MODEL slx_f5f0259db59d
CONFIG AbsTol = auto
CONFIG EnableMultiTasking = off
CONFIG FixedStep = auto
CONFIG MaxStep = auto
CONFIG MinStep = auto
CONFIG RelTol = 1e-3
CONFIG SampleTimeConstraint = Unconstrained
CONFIG SolverName = VariableStepAuto
CONFIG StartTime = 0.0
CONFIG StopTime = 8
BLOCK [Reference] AC Voltage Source3  REF=spsACVoltageSourceLib/AC Voltage Source
  LibrarySourceBlock = sps_lib/Sources/AC Voltage Source
  SourceBlock = spsACVoltageSourceLib/AC Voltage Source
  SourceType = AC Voltage Source
BLOCK [SubSystem] Brake Selector
BLOCK [From] Brake Selector/From1
  GotoTag = Brake
  TagVisibility = global
BLOCK [Inport] Brake Selector/Normally Close
  IconDisplay = Signal name
  Port = 2
BLOCK [Inport] Brake Selector/Normally Open
  IconDisplay = Signal name
BLOCK [Outport] Brake Selector/Out
  IconDisplay = Signal name
BLOCK [Switch] Brake Selector/Switch1
  InputSameDT = off
  SaturateOnIntegerOverflow = off
  Threshold = 0.5
BLOCK [SubSystem] Brake Selector1
BLOCK [From] Brake Selector1/From1
  GotoTag = Brake
  TagVisibility = global
BLOCK [Inport] Brake Selector1/Normally Close
  IconDisplay = Signal name
  Port = 2
BLOCK [Inport] Brake Selector1/Normally Open
  IconDisplay = Signal name
BLOCK [Outport] Brake Selector1/Out
  IconDisplay = Signal name
BLOCK [Switch] Brake Selector1/Switch1
  InputSameDT = off
  SaturateOnIntegerOverflow = off
  Threshold = 0.5
BLOCK [SubSystem] Brake Selector2
BLOCK [From] Brake Selector2/From1
  GotoTag = Brake
  TagVisibility = global
BLOCK [Inport] Brake Selector2/Normally Close
  IconDisplay = Signal name
  Port = 2
BLOCK [Inport] Brake Selector2/Normally Open
  IconDisplay = Signal name
BLOCK [Outport] Brake Selector2/Out
  IconDisplay = Signal name
BLOCK [Switch] Brake Selector2/Switch1
  InputSameDT = off
  SaturateOnIntegerOverflow = off
  Threshold = 0.5
BLOCK [SubSystem] Brake Selector3
BLOCK [From] Brake Selector3/From1
  GotoTag = Brake
  TagVisibility = global
BLOCK [Inport] Brake Selector3/Normally Close
  IconDisplay = Signal name
  Port = 2
BLOCK [Inport] Brake Selector3/Normally Open
  IconDisplay = Signal name
BLOCK [Outport] Brake Selector3/Out
  IconDisplay = Signal name
BLOCK [Switch] Brake Selector3/Switch1
  InputSameDT = off
  SaturateOnIntegerOverflow = off
  Threshold = 0.5
BLOCK [BusSelector] Bus Selector1
  OutputSignals = Electrical torque Te (n m),Speed wm (rad/s)
BLOCK [Constant] CCW Direction
  Value = 0
BLOCK [Constant] CW Direction
BLOCK [Constant] Constant
  Value = 0
BLOCK [Constant] Constant1
BLOCK [Constant] Constant2
  Value = 0.6
BLOCK [Constant] Constant3
BLOCK [Constant] Constant4
  Value = 0
BLOCK [Reference] Current Measurement  REF=spsCurrentMeasurementLib/Current Measurement
  LibrarySourceBlock = sps_lib/Sensors and Measurements/Current Measurement
  SourceBlock = spsCurrentMeasurementLib/Current Measurement
  SourceType = Current Measurement
  UserDataPersistent = on
BLOCK [Reference] Current Measurement1  REF=spsCurrentMeasurementLib/Current Measurement
  LibrarySourceBlock = sps_lib/Sensors and Measurements/Current Measurement
  SourceBlock = spsCurrentMeasurementLib/Current Measurement
  SourceType = Current Measurement
  UserDataPersistent = on
BLOCK [Reference] Current Measurement2  REF=spsCurrentMeasurementLib/Current Measurement
  LibrarySourceBlock = sps_lib/Sensors and Measurements/Current Measurement
  SourceBlock = spsCurrentMeasurementLib/Current Measurement
  SourceType = Current Measurement
  UserDataPersistent = on
BLOCK [Reference] Current Measurement3  REF=spsCurrentMeasurementLib/Current Measurement
  LibrarySourceBlock = sps_lib/Sensors and Measurements/Current Measurement
  NameLocation = right
  SourceBlock = spsCurrentMeasurementLib/Current Measurement
  SourceType = Current Measurement
  UserDataPersistent = on
BLOCK [Reference] Current Measurement4  REF=spsCurrentMeasurementLib/Current Measurement
  Commented = on
  LibrarySourceBlock = sps_lib/Sensors and Measurements/Current Measurement
  NameLocation = left
  SourceBlock = spsCurrentMeasurementLib/Current Measurement
  SourceType = Current Measurement
  UserDataPersistent = on
BLOCK [Reference] Current Measurement5  REF=spsCurrentMeasurementLib/Current Measurement
  LibrarySourceBlock = sps_lib/Sensors and Measurements/Current Measurement
  NameLocation = left
  SourceBlock = spsCurrentMeasurementLib/Current Measurement
  SourceType = Current Measurement
  UserDataPersistent = on
BLOCK [Reference] DC Machine1  REF=spsDCMachineLib/DC Machine
  LibrarySourceBlock = sps_lib/Electrical Machines/DC Machine
  SourceBlock = spsDCMachineLib/DC Machine
  SourceType = DC machine
BLOCK [Reference] DC Voltage Source  REF=spsDCVoltageSourceLib/DC Voltage Source
  LibrarySourceBlock = sps_lib/Sources/DC Voltage Source
  NameLocation = right
  SourceBlock = spsDCVoltageSourceLib/DC Voltage Source
  SourceType = DC Voltage Source
BLOCK [Reference] DC Voltage Source1  REF=spsDCVoltageSourceLib/DC Voltage Source
  Commented = on
  LibrarySourceBlock = sps_lib/Sources/DC Voltage Source
  SourceBlock = spsDCVoltageSourceLib/DC Voltage Source
  SourceType = DC Voltage Source
BLOCK [Reference] Diode1  REF=spsDiodeLib/Diode
  LibrarySourceBlock = sps_lib/Power Electronics/Diode
  NameLocation = right
  SourceBlock = spsDiodeLib/Diode
  SourceType = Diode
BLOCK [Reference] Diode2  REF=spsDiodeLib/Diode
  LibrarySourceBlock = sps_lib/Power Electronics/Diode
  NameLocation = right
  SourceBlock = spsDiodeLib/Diode
  SourceType = Diode
BLOCK [Reference] Diode3  REF=spsDiodeLib/Diode
  LibrarySourceBlock = sps_lib/Power Electronics/Diode
  NameLocation = right
  SourceBlock = spsDiodeLib/Diode
  SourceType = Diode
BLOCK [Reference] Diode4  REF=spsDiodeLib/Diode
  LibrarySourceBlock = sps_lib/Power Electronics/Diode
  NameLocation = right
  SourceBlock = spsDiodeLib/Diode
  SourceType = Diode
BLOCK [Reference] Diode5  REF=spsDiodeLib/Diode
  LibrarySourceBlock = sps_lib/Power Electronics/Diode
  NameLocation = right
  SourceBlock = spsDiodeLib/Diode
  SourceType = Diode
BLOCK [Reference] Diode6  REF=spsDiodeLib/Diode
  LibrarySourceBlock = sps_lib/Power Electronics/Diode
  NameLocation = right
  SourceBlock = spsDiodeLib/Diode
  SourceType = Diode
BLOCK [Reference] Diode7  REF=spsDiodeLib/Diode
  LibrarySourceBlock = sps_lib/Power Electronics/Diode
  NameLocation = right
  SourceBlock = spsDiodeLib/Diode
  SourceType = Diode
BLOCK [Reference] Diode8  REF=spsDiodeLib/Diode
  LibrarySourceBlock = sps_lib/Power Electronics/Diode
  NameLocation = right
  SourceBlock = spsDiodeLib/Diode
  SourceType = Diode
BLOCK [Display] Display
  Decimation = 1
BLOCK [Display] Display1
  Decimation = 1
BLOCK [Display] Display2
  Decimation = 1
BLOCK [Display] Display3
  Decimation = 1
BLOCK [Display] Display4
  Decimation = 1
BLOCK [Reference] First-Order Filter  REF=spsFirstOrderFilterLib/First-Order
Filter
  LibrarySourceBlock = sps_lib/Control/Filters/First-Order
Filter
  SourceBlock = spsFirstOrderFilterLib/First-Order
Filter
  SourceType = First-Order Filter
BLOCK [From] From
  GotoTag = Gate_Q1
  NameLocation = left
BLOCK [From] From1
  GotoTag = Gate_Q3
  NameLocation = left
BLOCK [From] From2
  GotoTag = Gate_Q4
  NameLocation = left
BLOCK [From] From3
  GotoTag = Gate_Q2
  NameLocation = left
BLOCK [From] From4
  GotoTag = Gate_Q1
BLOCK [From] From5
  GotoTag = Gate_Q2
BLOCK [From] From6
  GotoTag = Gate_Q3
BLOCK [From] From7
  GotoTag = Gate_Q4
BLOCK [From] From8
  GotoTag = Torque
  NameLocation = left
BLOCK [Scope] Gate Signals
  ActiveDisplayYMaximum = 1.2434958153271063
  ActiveDisplayYMinimum = -0.0065041846728933761
  DataLoggingVariableName = ScopeData21
  Floating = off
  GraphicalSettings = {"Style":{"BackgroundColor":[0.12941176470588237,0.12941176470588237,0.12941176470588237],"AxesColor":[0.07058823529411765,0.07058823529411765,0.07058823529411765],"LabelsColor":[0.8509803921568627,0.8509803921568627,0.8509803921568627],"PreserveColors":false,"Visible":[false,true,false,true],"LineStyle":["-","-","-","-"],"LineWidth":[1.5,1.5,1.5,1.5],"BarWidth":[0.9,0.9,0.9,0.9],"LineColor":["aut...<+2324ch>
  MultipleDisplayCache = [{"MaxYLimMag":1.125,"MaxYLimReal":1.2434958153271063,"MinYLimMag":0,"MinYLimReal":-0.0065041846728933761,"PlotAsMagnitudePhase":false,"ShowGrid":true,"ShowLegend":true,"Title":"%<SignalLabel>","YLabel":""}]
  NumInputPorts = 4
  ScopeFrameLocation = window
  ShowLegend = on
  WasSavedAsWebScope = on
  WindowPosition = [920.000000,418.000000,826.000000,527.000000,]
BLOCK [Goto] Goto
  GotoTag = Brake
  TagVisibility = global
BLOCK [Goto] Goto1
  GotoTag = Gate_Q1
BLOCK [Goto] Goto2
  GotoTag = Gate_Q3
BLOCK [Goto] Goto3
  GotoTag = Torque
BLOCK [Goto] Goto4
  GotoTag = Gate_Q2
BLOCK [Goto] Goto5
  GotoTag = Gate_Q4
BLOCK [Reference] Ground  REF=spsGroundLib/Ground
  LibrarySourceBlock = sps_lib/Utilities/Ground
  NameLocation = right
  SourceBlock = spsGroundLib/Ground
  SourceType = Ground
BLOCK [ManualSwitch] Manual Switch
BLOCK [ManualSwitch] Manual Switch1
  CurrentSetting = 0
BLOCK [ManualSwitch] Manual Switch2
BLOCK [Reference] Manual Variant Sink  REF=simulink/Signal
Routing/Manual
Variant Sink
  NameLocation = left
  SourceBlock = simulink/Signal
Routing/Manual
Variant Sink
  SourceType = ManualVariantSink
BLOCK [Reference] Mean  REF=spsMeanLib/Mean
  LibrarySourceBlock = sps_lib/Sensors and Measurements/Mean
  SourceBlock = spsMeanLib/Mean
  SourceType = Mean
BLOCK [Reference] Mean1  REF=spsMeanLib/Mean
  LibrarySourceBlock = sps_lib/Sensors and Measurements/Mean
  SourceBlock = spsMeanLib/Mean
  SourceType = Mean
BLOCK [Reference] Mean2  REF=spsMeanLib/Mean
  LibrarySourceBlock = sps_lib/Sensors and Measurements/Mean
  SourceBlock = spsMeanLib/Mean
  SourceType = Mean
BLOCK [Reference] Mean3  REF=spsMeanLib/Mean
  LibrarySourceBlock = sps_lib/Sensors and Measurements/Mean
  SourceBlock = spsMeanLib/Mean
  SourceType = Mean
BLOCK [Reference] Mosfet5  REF=spsMosfetLib/Mosfet
  LibrarySourceBlock = sps_lib/Power Electronics/Mosfet
  NameLocation = left
  SourceBlock = spsMosfetLib/Mosfet
  SourceType = Mosfet
BLOCK [Logic] NOT
  AllPortsSameDT = off
  IconShape = distinctive
  Operator = NOT
  OutDataTypeStr = boolean
BLOCK [Reference] PWM Generator  REF=eePwmGenerator/PWM Generator
  LibrarySourceBlock = ee_sl_lib/Pulse Width
Modulation/PWM Generator
  SourceBlock = eePwmGenerator/PWM Generator
  SourceType = PWM Generator
BLOCK [Reference] PWM Generator1  REF=eePwmGenerator/PWM Generator
  LibrarySourceBlock = ee_sl_lib/Pulse Width
Modulation/PWM Generator
  SourceBlock = eePwmGenerator/PWM Generator
  SourceType = PWM Generator
BLOCK [Product] Product
BLOCK [Product] Product1
BLOCK [Product] Product2
BLOCK [Product] Product3
BLOCK [Product] Product4
BLOCK [Product] Product5
BLOCK [Reference] Q1  REF=spsMosfetLib/Mosfet
  LibrarySourceBlock = sps_lib/Power Electronics/Mosfet
  NameLocation = left
  SourceBlock = spsMosfetLib/Mosfet
  SourceType = Mosfet
BLOCK [Reference] Q2  REF=spsMosfetLib/Mosfet
  LibrarySourceBlock = sps_lib/Power Electronics/Mosfet
  NameLocation = left
  SourceBlock = spsMosfetLib/Mosfet
  SourceType = Mosfet
BLOCK [Reference] Q3  REF=spsMosfetLib/Mosfet
  LibrarySourceBlock = sps_lib/Power Electronics/Mosfet
  NameLocation = left
  SourceBlock = spsMosfetLib/Mosfet
  SourceType = Mosfet
BLOCK [Reference] Q4  REF=spsMosfetLib/Mosfet
  LibrarySourceBlock = sps_lib/Power Electronics/Mosfet
  NameLocation = left
  SourceBlock = spsMosfetLib/Mosfet
  SourceType = Mosfet
BLOCK [Reference] Ramp  REF=simulink/Sources/Ramp
  SourceBlock = simulink/Sources/Ramp
  SourceType = Ramp
BLOCK [Reference] Ramp1  REF=simulink/Sources/Ramp
  SourceBlock = simulink/Sources/Ramp
  SourceType = Ramp
BLOCK [Reference] Ramp2  REF=simulink/Sources/Ramp
  SourceBlock = simulink/Sources/Ramp
  SourceType = Ramp
BLOCK [Saturate] Saturation
  LowerLimit = 0
  UpperLimit = 20
BLOCK [Saturate] Saturation1
  LowerLimit = 0
  UpperLimit = 0.8
BLOCK [Saturate] Saturation2
  LowerLimit = 0
  UpperLimit = 1
BLOCK [Scope] Scope
  ActiveDisplayYMaximum = 104.1740277954152
  ActiveDisplayYMinimum = -11.583479260065536
  DataLoggingVariableName = ScopeData2
  Floating = off
  GraphicalSettings = {"AxesScalingProperties":{"AlignXAxis":"Center","AlignYAxis":"Center","AutoScaleXAxisLimits":false,"AxesScaling":"Manual","AxesScalingNumUpdates":10,"ExpandOnly":true,"ScaleAxesLimitsAtStop":false,"XAxisDataRange":100,"YAxisDataRange":80},"DisplayProperties":{"ColorOrder":["auto","auto","auto","auto","auto","auto","auto","auto","auto","auto","auto","auto","auto","auto","auto","auto","auto","auto",...<+2160ch>
  MultipleDisplayCache = [{"MaxYLimMag":104.1740277954152,"MaxYLimReal":104.1740277954152,"MinYLimMag":0,"MinYLimReal":-11.583479260065536,"PlotAsMagnitudePhase":false,"ShowGrid":true,"ShowLegend":true,"Title":"%<SignalLabel>","YLabel":""}]
  NameLocation = left
  NumInputPorts = 1
  ScopeFrameLocation = window
  ShowLegend = on
  Visible = on
  WasSavedAsWebScope = on
  WindowPosition = [0.000000,32.000000,1920.000000,1017.000000,]
BLOCK [Scope] Scope1
  ActiveDisplayYMaximum = 256.22277966423093
  ActiveDisplayYMinimum = -28.46919774047009
  Floating = off
  GraphicalSettings = {"AxesScalingProperties":{"AlignXAxis":"Center","AlignYAxis":"Center","AutoScaleXAxisLimits":false,"AxesScaling":"Manual","AxesScalingNumUpdates":10,"ExpandOnly":true,"ScaleAxesLimitsAtStop":false,"XAxisDataRange":100,"YAxisDataRange":80},"DisplayProperties":{"ColorOrder":["auto","auto","auto","auto","auto","auto","auto","auto","auto","auto","auto","auto","auto","auto","auto","auto","auto","auto",...<+2032ch>  <repeated x3 — deduplicated>
  MultipleDisplayCache = [{"MaxYLimMag":256.22277966423093,"MaxYLimReal":256.22277966423093,"MinYLimMag":0,"MinYLimReal":-28.46919774047009,"PlotAsMagnitudePhase":false,"ShowGrid":true,"ShowLegend":false,"Title":"%<SignalLabel>","YLabel":""}]
  NumInputPorts = 1
  ScopeFrameLocation = window
  WasSavedAsWebScope = on
  WindowPosition = [1.000000,41.000000,1920.000000,1017.000000,]
BLOCK [Scope] Scope10
  ActiveDisplayYMaximum = 1429.223755324701
  ActiveDisplayYMinimum = 624.50186928798541
  DataLoggingVariableName = ScopeData10
  Floating = off
  GraphicalSettings = {"AxesScalingProperties":{"AlignXAxis":"Center","AlignYAxis":"Center","AutoScaleXAxisLimits":false,"AxesScaling":"Manual","AxesScalingNumUpdates":10,"ExpandOnly":true,"ScaleAxesLimitsAtStop":false,"XAxisDataRange":100,"YAxisDataRange":80},"DisplayProperties":{"ColorOrder":["auto","auto","auto","auto","auto","auto","auto","auto","auto","auto","auto","auto","auto","auto","auto","auto","auto","auto",...<+1914ch>
  MultipleDisplayCache = [{"MaxYLimMag":3801.8138292180056,"MaxYLimReal":1429.223755324701,"MinYLimMag":0,"MinYLimReal":624.50186928798541,"PlotAsMagnitudePhase":false,"ShowGrid":true,"ShowLegend":false,"Title":"%<SignalLabel>","YLabel":""}]
  NumInputPorts = 1
  ScopeFrameLocation = window
  WasSavedAsWebScope = on
  WindowPosition = [1.000000,41.000000,1920.000000,1017.000000,]
BLOCK [Scope] Scope11
  ActiveDisplayYMaximum = 10839.355284849147
  ActiveDisplayYMinimum = -2401.1873049076858
  DataLoggingVariableName = ScopeData12
  Floating = off
  GraphicalSettings = {"AxesScalingProperties":{"AlignXAxis":"Center","AlignYAxis":"Center","AutoScaleXAxisLimits":false,"AxesScaling":"Manual","AxesScalingNumUpdates":10,"ExpandOnly":true,"ScaleAxesLimitsAtStop":false,"XAxisDataRange":100,"YAxisDataRange":80},"DisplayProperties":{"ColorOrder":["auto","auto","auto","auto","auto","auto","auto","auto","auto","auto","auto","auto","auto","auto","auto","auto","auto","auto",...<+2024ch>
  MultipleDisplayCache = [{"MaxYLimMag":23271.969727015163,"MaxYLimReal":10839.355284849147,"MinYLimMag":0,"MinYLimReal":-2401.1873049076858,"PlotAsMagnitudePhase":false,"ShowGrid":true,"ShowLegend":false,"Title":"%<SignalLabel>","YLabel":""}]
  NumInputPorts = 1
  ScopeFrameLocation = window
  WasSavedAsWebScope = on
  WindowPosition = [783.000000,533.000000,560.000000,420.000000,]
BLOCK [Scope] Scope12
  ActiveDisplayYMaximum = 104.03628291708009
  ActiveDisplayYMinimum = -11.566622282825097
  DataLoggingVariableName = ScopeData11
  Floating = off
  GraphicalSettings = {"Style":{"BackgroundColor":[0.12941176470588237,0.12941176470588237,0.12941176470588237],"AxesColor":[0.07058823529411765,0.07058823529411765,0.07058823529411765],"LabelsColor":[0.8509803921568627,0.8509803921568627,0.8509803921568627],"PreserveColors":false,"Visible":[true],"LineStyle":["-"],"LineWidth":[1.5],"BarWidth":[0.9],"LineColor":["auto"],"LineFaceAlpha":[1],"LineEdgeAlpha":[1],"Marker":...<+2017ch>
  MultipleDisplayCache = [{"MaxYLimMag":104.03628291708009,"MaxYLimReal":104.03628291708009,"MinYLimMag":0,"MinYLimReal":-11.566622282825097,"PlotAsMagnitudePhase":false,"ShowGrid":true,"ShowLegend":false,"Title":"%<SignalLabel>","YLabel":""}]
  NameLocation = right
  NumInputPorts = 1
  ScopeFrameLocation = window
  WasSavedAsWebScope = on
  WindowPosition = [0.000000,32.000000,1536.000000,801.000000,]
BLOCK [Scope] Scope13
  DataLoggingVariableName = ScopeData13
  Floating = off
  GraphicalSettings = {"GraphicalSettings":{"LegacySettings":true,"Style":{"Style":{"PlotType":"Auto"}}}}
  NumInputPorts = 1
  WasSavedAsWebScope = on
BLOCK [Scope] Scope14
  ActiveDisplayYMaximum = 2945.0127128560962
  ActiveDisplayYMinimum = 762.41218453396561
  DataLoggingVariableName = ScopeData14
  Floating = off
  GraphicalSettings = {"AxesScalingProperties":{"AlignXAxis":"Center","AlignYAxis":"Center","AutoScaleXAxisLimits":false,"AxesScaling":"Manual","AxesScalingNumUpdates":10,"ExpandOnly":true,"ScaleAxesLimitsAtStop":false,"XAxisDataRange":100,"YAxisDataRange":80},"DisplayProperties":{"ColorOrder":["auto","auto","auto","auto","auto","auto","auto","auto","auto","auto","auto","auto","auto","auto","auto","auto","auto","auto",...<+2026ch>
  MultipleDisplayCache = [{"MaxYLimMag":23271.969727015163,"MaxYLimReal":2945.0127128560962,"MinYLimMag":0,"MinYLimReal":762.41218453396561,"PlotAsMagnitudePhase":false,"ShowGrid":true,"ShowLegend":false,"Title":"%<SignalLabel>","YLabel":""}]
  NumInputPorts = 1
  ScopeFrameLocation = window
  WasSavedAsWebScope = on
  WindowPosition = [1.000000,41.000000,1920.000000,1017.000000,]
BLOCK [Scope] Scope15
  DataLoggingVariableName = ScopeData15
  Floating = off
  GraphicalSettings = {"GraphicalSettings":{"LegacySettings":true,"Style":{"Style":{"PlotType":"Auto"}}}}
  NumInputPorts = 1
  WasSavedAsWebScope = on
BLOCK [Scope] Scope16
  ActiveDisplayYMaximum = 137.54032935552146
  ActiveDisplayYMinimum = -15.282258817280159
  DataLoggingVariableName = ScopeData16
  Floating = off
  GraphicalSettings = {"Style":{"BackgroundColor":[0.12941176470588237,0.12941176470588237,0.12941176470588237],"AxesColor":[0.07058823529411765,0.07058823529411765,0.07058823529411765],"LabelsColor":[0.8509803921568627,0.8509803921568627,0.8509803921568627],"PreserveColors":false,"Visible":[true],"LineStyle":["-"],"LineWidth":[1.5],"BarWidth":[0.9],"LineColor":["auto"],"LineFaceAlpha":[1],"LineEdgeAlpha":[1],"Marker":...<+2338ch>
  MultipleDisplayCache = [{"MaxYLimMag":137.54032935552146,"MaxYLimReal":137.54032935552146,"MinYLimMag":0,"MinYLimReal":-15.282258817280159,"PlotAsMagnitudePhase":false,"ShowGrid":true,"ShowLegend":false,"Title":"%<SignalLabel>","YLabel":""}]
  NumInputPorts = 1
  ScopeFrameLocation = window
  WasSavedAsWebScope = on
  WindowPosition = [2.000000,42.000000,1918.000000,1008.000000,]
BLOCK [Scope] Scope17
  ActiveDisplayYMaximum = 226.2370362043749
  ActiveDisplayYMinimum = -36.761209497993441
  DataLoggingVariableName = ScopeData17
  Floating = off
  GraphicalSettings = {"Style":{"BackgroundColor":[0.12941176470588237,0.12941176470588237,0.12941176470588237],"AxesColor":[0.07058823529411765,0.07058823529411765,0.07058823529411765],"LabelsColor":[0.8509803921568627,0.8509803921568627,0.8509803921568627],"PreserveColors":false,"Visible":[true],"LineStyle":["-"],"LineWidth":[1.5],"BarWidth":[0.9],"LineColor":["auto"],"LineFaceAlpha":[1],"LineEdgeAlpha":[1],"Marker":...<+2019ch>
  MultipleDisplayCache = [{"MaxYLimMag":226.2370362043749,"MaxYLimReal":226.2370362043749,"MinYLimMag":0,"MinYLimReal":-36.761209497993441,"PlotAsMagnitudePhase":false,"ShowGrid":true,"ShowLegend":false,"Title":"%<SignalLabel>","YLabel":""}]
  NumInputPorts = 1
  ScopeFrameLocation = window
  WasSavedAsWebScope = on
  WindowPosition = [2.000000,42.000000,1918.000000,1008.000000,]
BLOCK [Scope] Scope18
  DataLoggingVariableName = ScopeData18
  Floating = off
  GraphicalSettings = {"GraphicalSettings":{"LegacySettings":true,"Style":{"Style":{"PlotType":"Auto"}}}}
  NameLocation = left
  NumInputPorts = 1
  WasSavedAsWebScope = on
BLOCK [Scope] Scope19
  ActiveDisplayYMaximum = 103.81128270332889
  ActiveDisplayYMinimum = -12.603657312689416
  DataLoggingVariableName = ScopeData19
  Floating = off
  GraphicalSettings = {"Style":{"BackgroundColor":[0.12941176470588237,0.12941176470588237,0.12941176470588237],"AxesColor":[0.07058823529411765,0.07058823529411765,0.07058823529411765],"LabelsColor":[0.8509803921568627,0.8509803921568627,0.8509803921568627],"PreserveColors":false,"Visible":[true],"LineStyle":["-"],"LineWidth":[1.5],"BarWidth":[0.9],"LineColor":["auto"],"LineFaceAlpha":[1],"LineEdgeAlpha":[1],"Marker":...<+1920ch>
  MultipleDisplayCache = [{"MaxYLimMag":103.81128270332889,"MaxYLimReal":103.81128270332889,"MinYLimMag":0,"MinYLimReal":-12.603657312689416,"PlotAsMagnitudePhase":false,"ShowGrid":true,"ShowLegend":false,"Title":"%<SignalLabel>","YLabel":""}]
  NameLocation = top
  NumInputPorts = 1
  ScopeFrameLocation = window
  WasSavedAsWebScope = on
  WindowPosition = [680.000000,330.000000,560.000000,420.000000,]
BLOCK [Scope] Scope2
  ActiveDisplayYMaximum = 25.20951403026401
  ActiveDisplayYMinimum = -226.88562627237616
  DataLoggingVariableName = ScopeData3
  Floating = off
  GraphicalSettings = {"Style":{"BackgroundColor":[0.12941176470588237,0.12941176470588237,0.12941176470588237],"AxesColor":[0.07058823529411765,0.07058823529411765,0.07058823529411765],"LabelsColor":[0.8509803921568627,0.8509803921568627,0.8509803921568627],"PreserveColors":false,"Visible":[true,true],"LineStyle":["-","-"],"LineWidth":[1.5,1.5],"BarWidth":[0.9,0.9],"LineColor":["auto","auto"],"LineFaceAlpha":[1,1],"Li...<+2069ch>
  MultipleDisplayCache = [{"MaxYLimMag":226.88562627237616,"MaxYLimReal":25.20951403026401,"MinYLimMag":0,"MinYLimReal":-226.88562627237616,"PlotAsMagnitudePhase":false,"ShowGrid":true,"ShowLegend":false,"Title":"%<SignalLabel>","YLabel":""}]
  NameLocation = right
  NumInputPorts = 1
  ScopeFrameLocation = window
  WasSavedAsWebScope = on
  WindowPosition = [488.000000,222.000000,560.000000,420.000000,]
BLOCK [Scope] Scope20
  ActiveDisplayYMaximum = 1.125
  ActiveDisplayYMinimum = -0.12499999999999997
  DataLoggingVariableName = ScopeData20
  Floating = off
  GraphicalSettings = {"AxesScalingProperties":{"AlignXAxis":"Center","AlignYAxis":"Center","AutoScaleXAxisLimits":false,"AxesScaling":"Manual","AxesScalingNumUpdates":10,"ExpandOnly":true,"ScaleAxesLimitsAtStop":false,"XAxisDataRange":100,"YAxisDataRange":80},"DisplayProperties":{"ColorOrder":["auto","auto","auto","auto","auto","auto","auto","auto","auto","auto","auto","auto","auto","auto","auto","auto","auto","auto",...<+1970ch>
  MultipleDisplayCache = [{"MaxYLimMag":1.125,"MaxYLimReal":1.125,"MinYLimMag":0,"MinYLimReal":-0.12499999999999997,"PlotAsMagnitudePhase":false,"ShowGrid":true,"ShowLegend":false,"Title":"%<SignalLabel>","YLabel":""}]
  NumInputPorts = 1
  ScopeFrameLocation = window
  WasSavedAsWebScope = on
  WindowPosition = [1.000000,41.000000,1920.000000,1017.000000,]
BLOCK [Scope] Scope21
  ActiveDisplayYMaximum = 211.04566043540314
  ActiveDisplayYMinimum = -1899.3717072203649
  DataLoggingVariableName = ScopeData9
  Floating = off
  GraphicalSettings = {"AxesScalingProperties":{"AlignXAxis":"Center","AlignYAxis":"Center","AutoScaleXAxisLimits":false,"AxesScaling":"Manual","AxesScalingNumUpdates":10,"ExpandOnly":true,"ScaleAxesLimitsAtStop":false,"XAxisDataRange":100,"YAxisDataRange":80},"DisplayProperties":{"ColorOrder":["auto","auto","auto","auto","auto","auto","auto","auto","auto","auto","auto","auto","auto","auto","auto","auto","auto","auto",...<+2205ch>
  MultipleDisplayCache = [{"MaxYLimMag":1899.3717072203649,"MaxYLimReal":211.04566043540314,"MinYLimMag":0,"MinYLimReal":-1899.3717072203649,"PlotAsMagnitudePhase":false,"ShowGrid":true,"ShowLegend":false,"Title":"%<SignalLabel>","YLabel":""}]
  NumInputPorts = 1
  ScopeFrameLocation = window
  WasSavedAsWebScope = on
  WindowPosition = [1.000000,41.000000,1920.000000,1017.000000,]
BLOCK [Scope] Scope22
  ActiveDisplayYMaximum = 43.751360629299874
  ActiveDisplayYMinimum = -4.8702002164060625
  DataLoggingVariableName = ScopeData23
  Floating = off
  GraphicalSettings = {"Style":{"BackgroundColor":[0.12941176470588237,0.12941176470588237,0.12941176470588237],"AxesColor":[0.07058823529411765,0.07058823529411765,0.07058823529411765],"LabelsColor":[0.8509803921568627,0.8509803921568627,0.8509803921568627],"PreserveColors":false,"Visible":[true],"LineStyle":["-"],"LineWidth":[1.5],"BarWidth":[0.9],"LineColor":["auto"],"LineFaceAlpha":[1],"LineEdgeAlpha":[1],"Marker":...<+2025ch>
  MultipleDisplayCache = [{"MaxYLimMag":43.751360629299874,"MaxYLimReal":43.751360629299874,"MinYLimMag":0,"MinYLimReal":-4.8702002164060625,"PlotAsMagnitudePhase":false,"ShowGrid":true,"ShowLegend":false,"Title":"%<SignalLabel>","YLabel":""}]
  NameLocation = right
  NumInputPorts = 1
  ScopeFrameLocation = window
  WasSavedAsWebScope = on
  WindowPosition = [1.000000,41.000000,1920.000000,1017.000000,]
BLOCK [Scope] Scope23
  ActiveDisplayYMaximum = 71.245138524934077
  ActiveDisplayYMinimum = -145.42462200714976
  Commented = on
  DataLoggingVariableName = ScopeData24
  Floating = off
  GraphicalSettings = {"AxesScalingProperties":{"AlignXAxis":"Center","AlignYAxis":"Center","AutoScaleXAxisLimits":false,"AxesScaling":"Manual","AxesScalingNumUpdates":10,"ExpandOnly":true,"ScaleAxesLimitsAtStop":false,"XAxisDataRange":100,"YAxisDataRange":80},"DisplayProperties":{"ColorOrder":["auto","auto","auto","auto","auto","auto","auto","auto","auto","auto","auto","auto","auto","auto","auto","auto","auto","auto",...<+1936ch>
  MultipleDisplayCache = [{"MaxYLimMag":145.42462200714976,"MaxYLimReal":71.245138524934077,"MinYLimMag":0,"MinYLimReal":-145.42462200714976,"PlotAsMagnitudePhase":false,"ShowGrid":true,"ShowLegend":false,"Title":"%<SignalLabel>","YLabel":""}]
  NumInputPorts = 1
  ScopeFrameLocation = window
  WasSavedAsWebScope = on
  WindowPosition = [1.000000,41.000000,1920.000000,1017.000000,]
BLOCK [Scope] Scope24
  ActiveDisplayYMaximum = 197.18570910939735
  ActiveDisplayYMinimum = -110.97493026864629
  DataLoggingVariableName = ScopeData25
  Floating = off
  MultipleDisplayCache = [{"MaxYLimMag":184.87259500897878,"MaxYLimReal":197.18570910939735,"MinYLimMag":0,"MinYLimReal":-110.97493026864629,"PlotAsMagnitudePhase":false,"ShowGrid":true,"ShowLegend":false,"Title":"%<SignalLabel>","YLabel":""}]
  NameLocation = top
  NumInputPorts = 1
  ScopeFrameLocation = window
  WasSavedAsWebScope = on
  WindowPosition = [1.000000,41.000000,1920.000000,1017.000000,]
BLOCK [Scope] Scope25
  ActiveDisplayYMaximum = 173.45713764140422
  ActiveDisplayYMinimum = -19.273015293489355
  DataLoggingVariableName = ScopeData26
  Floating = off
  GraphicalSettings = {"AxesScalingProperties":{"AlignXAxis":"Center","AlignYAxis":"Center","AutoScaleXAxisLimits":false,"AxesScaling":"Manual","AxesScalingNumUpdates":10,"ExpandOnly":true,"ScaleAxesLimitsAtStop":false,"XAxisDataRange":100,"YAxisDataRange":80},"Cursors":{"CursorChannels":["auto","auto"],"Enabled":false,"Horizontal":true,"LinkToWaveform":true,"LockSpacing":false,"ShowMeasurement":true,"ShowPanel":false,...<+2674ch>
  MultipleDisplayCache = [{"MaxYLimMag":173.45713764140422,"MaxYLimReal":173.45713764140422,"MinYLimMag":0,"MinYLimReal":-19.273015293489355,"PlotAsMagnitudePhase":false,"ShowGrid":true,"ShowLegend":true,"Title":"%<SignalLabel>","YLabel":""}]
  NameLocation = right
  NumInputPorts = 1
  ScopeFrameLocation = window
  ShowLegend = on
  WasSavedAsWebScope = on
  WindowPosition = [1.000000,41.000000,1920.000000,1017.000000,]
BLOCK [Scope] Scope3
  ActiveDisplayYMaximum = 132.92248346873072
  ActiveDisplayYMinimum = -122.00523332078208
  DataLoggingVariableName = ScopeData4
  Floating = off
  GraphicalSettings = {"Style":{"BackgroundColor":[0.12941176470588237,0.12941176470588237,0.12941176470588237],"AxesColor":[0.07058823529411765,0.07058823529411765,0.07058823529411765],"LabelsColor":[0.8509803921568627,0.8509803921568627,0.8509803921568627],"PreserveColors":false,"Visible":[true,false],"LineStyle":["-","-"],"LineWidth":[1.5,1.5],"BarWidth":[0.9,0.9],"LineColor":["auto","auto"],"LineFaceAlpha":[1,1],"L...<+2153ch>
  MultipleDisplayCache = [{"MaxYLimMag":132.92248346873072,"MaxYLimReal":132.92248346873072,"MinYLimMag":0,"MinYLimReal":-122.00523332078208,"PlotAsMagnitudePhase":false,"ShowGrid":true,"ShowLegend":true,"Title":"%<SignalLabel>","YLabel":""}]
  NameLocation = left
  NumInputPorts = 1
  ScopeFrameLocation = window
  ShowLegend = on
  WasSavedAsWebScope = on
  WindowPosition = [1.000000,41.000000,1920.000000,1017.000000,]
BLOCK [Scope] Scope4
  ActiveDisplayYMaximum = 243.58123391583604
  ActiveDisplayYMinimum = -65.687848106790781
  DataLoggingVariableName = ScopeData1
  Floating = off
  GraphicalSettings = {"Style":{"BackgroundColor":[0.12941176470588237,0.12941176470588237,0.12941176470588237],"AxesColor":[0.07058823529411765,0.07058823529411765,0.07058823529411765],"LabelsColor":[0.8509803921568627,0.8509803921568627,0.8509803921568627],"PreserveColors":false,"Visible":[true],"LineStyle":["-"],"LineWidth":[1.5],"BarWidth":[0.9],"LineColor":["auto"],"LineFaceAlpha":[1],"LineEdgeAlpha":[1],"Marker":...<+2039ch>
  MultipleDisplayCache = [{"MaxYLimMag":243.58123391583604,"MaxYLimReal":243.58123391583604,"MinYLimMag":0,"MinYLimReal":-65.687848106790781,"PlotAsMagnitudePhase":false,"ShowGrid":true,"ShowLegend":false,"Title":"%<SignalLabel>","YLabel":""}]
  NumInputPorts = 1
  ScopeFrameLocation = window
  WasSavedAsWebScope = on
  WindowPosition = [1.000000,41.000000,1920.000000,1017.000000,]
BLOCK [Scope] Scope5
  ActiveDisplayYMaximum = 7.0075960496809362
  ActiveDisplayYMinimum = -1.20703950016334
  DataLoggingVariableName = ScopeData6
  Floating = off
  GraphicalSettings = {"Style":{"BackgroundColor":[0.12941176470588237,0.12941176470588237,0.12941176470588237],"AxesColor":[0.07058823529411765,0.07058823529411765,0.07058823529411765],"LabelsColor":[0.8509803921568627,0.8509803921568627,0.8509803921568627],"PreserveColors":false,"Visible":[true,true],"LineStyle":["-","-"],"LineWidth":[1.5,1.5],"BarWidth":[0.9,0.9],"LineColor":["auto","auto"],"LineFaceAlpha":[1,1],"Li...<+2168ch>
  MultipleDisplayCache = [{"MaxYLimMag":126.86904472662312,"MaxYLimReal":7.0075960496809362,"MinYLimMag":0,"MinYLimReal":-1.20703950016334,"PlotAsMagnitudePhase":false,"ShowGrid":true,"ShowLegend":false,"Title":"%<SignalLabel>","YLabel":""}]
  NameLocation = left
  NumInputPorts = 1
  ScopeFrameLocation = window
  WasSavedAsWebScope = on
  WindowPosition = [0.000000,32.000000,1536.000000,801.000000,]
BLOCK [Scope] Scope6
  ActiveDisplayYMaximum = 71.8134310936752
  ActiveDisplayYMinimum = -7.9782501074375674
  DataLoggingVariableName = ScopeData5
  Floating = off
  GraphicalSettings = {"Style":{"BackgroundColor":[0.12941176470588237,0.12941176470588237,0.12941176470588237],"AxesColor":[0.07058823529411765,0.07058823529411765,0.07058823529411765],"LabelsColor":[0.8509803921568627,0.8509803921568627,0.8509803921568627],"PreserveColors":false,"Visible":[true],"LineStyle":["-"],"LineWidth":[1.5],"BarWidth":[0.9],"LineColor":["auto"],"LineFaceAlpha":[1],"LineEdgeAlpha":[1],"Marker":...<+2011ch>
  MultipleDisplayCache = [{"MaxYLimMag":71.8134310936752,"MaxYLimReal":71.8134310936752,"MinYLimMag":0,"MinYLimReal":-7.9782501074375674,"PlotAsMagnitudePhase":false,"ShowGrid":true,"ShowLegend":false,"Title":"%<SignalLabel>","YLabel":""}]
  NumInputPorts = 1
  ScopeFrameLocation = window
  WasSavedAsWebScope = on
  WindowPosition = [392.000000,303.000000,1119.000000,637.000000,]
BLOCK [Scope] Scope7
  ActiveDisplayYMaximum = 171.40567773098573
  ActiveDisplayYMinimum = -170.79208981594385
  DataLoggingVariableName = ScopeData7
  Floating = off
  MultipleDisplayCache = [{"MaxYLimMag":171.40567773098573,"MaxYLimReal":171.40567773098573,"MinYLimMag":0,"MinYLimReal":-170.79208981594385,"PlotAsMagnitudePhase":false,"ShowGrid":true,"ShowLegend":false,"Title":"%<SignalLabel>","YLabel":""}]
  NameLocation = right
  NumInputPorts = 1
  ScopeFrameLocation = window
  WasSavedAsWebScope = on
  WindowPosition = [1.000000,41.000000,1920.000000,1017.000000,]
BLOCK [Scope] Scope8
  ActiveDisplayYMaximum = 140.46232304628771
  ActiveDisplayYMinimum = -136.4523697158933
  DataLoggingVariableName = ScopeData8
  Floating = off
  GraphicalSettings = {"Style":{"BackgroundColor":[0.12941176470588237,0.12941176470588237,0.12941176470588237],"AxesColor":[0.07058823529411765,0.07058823529411765,0.07058823529411765],"LabelsColor":[0.8509803921568627,0.8509803921568627,0.8509803921568627],"PreserveColors":false,"Visible":[true],"LineStyle":["-"],"LineWidth":[1.5],"BarWidth":[0.9],"LineColor":["auto"],"LineFaceAlpha":[1],"LineEdgeAlpha":[1],"Marker":...<+2019ch>
  MultipleDisplayCache = [{"MaxYLimMag":140.46232304628771,"MaxYLimReal":140.46232304628771,"MinYLimMag":0,"MinYLimReal":-136.4523697158933,"PlotAsMagnitudePhase":false,"ShowGrid":true,"ShowLegend":false,"Title":"%<SignalLabel>","YLabel":""}]
  NameLocation = right
  NumInputPorts = 1
  ScopeFrameLocation = window
  WasSavedAsWebScope = on
  WindowPosition = [238.000000,236.000000,1183.000000,720.000000,]
BLOCK [Scope] Scope9
  ActiveDisplayYMaximum = 243.07898503401125
  ActiveDisplayYMinimum = -2178.2019033970919
  DataLoggingVariableName = ScopeData22
  Floating = off
  GraphicalSettings = {"Style":{"BackgroundColor":[0.12941176470588237,0.12941176470588237,0.12941176470588237],"AxesColor":[0.07058823529411765,0.07058823529411765,0.07058823529411765],"LabelsColor":[0.8509803921568627,0.8509803921568627,0.8509803921568627],"PreserveColors":false,"Visible":[true],"LineStyle":["-"],"LineWidth":[1.5],"BarWidth":[0.9],"LineColor":["auto"],"LineFaceAlpha":[1],"LineEdgeAlpha":[1],"Marker":...<+2035ch>
  MultipleDisplayCache = [{"MaxYLimMag":2178.2019033970919,"MaxYLimReal":243.07898503401125,"MinYLimMag":0,"MinYLimReal":-2178.2019033970919,"PlotAsMagnitudePhase":false,"ShowGrid":true,"ShowLegend":false,"Title":"%<SignalLabel>","YLabel":""}]
  NumInputPorts = 1
  ScopeFrameLocation = window
  WasSavedAsWebScope = on
  WindowPosition = [1.000000,41.000000,1920.000000,1017.000000,]
BLOCK [Reference] Series RLC Branch1  REF=spsSeriesRLCBranchLib/Series RLC Branch
  LibrarySourceBlock = sps_lib/Passives/Series RLC Branch
  SourceBlock = spsSeriesRLCBranchLib/Series RLC Branch
  SourceType = Series RLC Branch
BLOCK [Reference] Series RLC Branch2  REF=spsSeriesRLCBranchLib/Series RLC Branch
  LibrarySourceBlock = sps_lib/Passives/Series RLC Branch
  NameLocation = left
  SourceBlock = spsSeriesRLCBranchLib/Series RLC Branch
  SourceType = Series RLC Branch
BLOCK [Reference] Series RLC Branch3  REF=spsSeriesRLCBranchLib/Series RLC Branch
  LibrarySourceBlock = sps_lib/Passives/Series RLC Branch
  NameLocation = left
  SourceBlock = spsSeriesRLCBranchLib/Series RLC Branch
  SourceType = Series RLC Branch
BLOCK [Reference] Series RLC Branch4  REF=spsSeriesRLCBranchLib/Series RLC Branch
  LibrarySourceBlock = sps_lib/Passives/Series RLC Branch
  NameLocation = left
  SourceBlock = spsSeriesRLCBranchLib/Series RLC Branch
  SourceType = Series RLC Branch
BLOCK [Step] Step
  SampleTime = 0
  Time = 3.5
BLOCK [Reference] Voltage Measurement  REF=spsVoltageMeasurementLib/Voltage Measurement
  LibrarySourceBlock = sps_lib/Sensors and Measurements/Voltage Measurement
  SourceBlock = spsVoltageMeasurementLib/Voltage Measurement
  SourceType = Voltage Measurement
  UserDataPersistent = on
BLOCK [Reference] Voltage Measurement1  REF=spsVoltageMeasurementLib/Voltage Measurement
  LibrarySourceBlock = sps_lib/Sensors and Measurements/Voltage Measurement
  SourceBlock = spsVoltageMeasurementLib/Voltage Measurement
  SourceType = Voltage Measurement
  UserDataPersistent = on
BLOCK [Reference] Voltage Measurement2  REF=spsVoltageMeasurementLib/Voltage Measurement
  LibrarySourceBlock = sps_lib/Sensors and Measurements/Voltage Measurement
  SourceBlock = spsVoltageMeasurementLib/Voltage Measurement
  SourceType = Voltage Measurement
  UserDataPersistent = on
BLOCK [Reference] powergui2  REF=sps_lib/powergui
  LibrarySourceBlock = sps_lib/powergui
  Priority = 1
  SourceBlock = sps_lib/powergui
  SourceType = PSB option menu block
LINE AC Voltage Source3:rconn -> Current Measurement1:lconn
LINE Brake Selector/From1:1 -> Brake Selector/Switch1:2
LINE Brake Selector/Normally Close:1 -> Brake Selector/Switch1:3
LINE Brake Selector/Normally Open:1 -> Brake Selector/Switch1:1
LINE Brake Selector/Switch1:1 -> Brake Selector/Out:1
LINE Brake Selector1/From1:1 -> Brake Selector1/Switch1:2
LINE Brake Selector1/Normally Close:1 -> Brake Selector1/Switch1:3
LINE Brake Selector1/Normally Open:1 -> Brake Selector1/Switch1:1
LINE Brake Selector1/Switch1:1 -> Brake Selector1/Out:1
LINE Brake Selector1:1 -> Goto4:1
LINE Brake Selector2/From1:1 -> Brake Selector2/Switch1:2
LINE Brake Selector2/Normally Close:1 -> Brake Selector2/Switch1:3
LINE Brake Selector2/Normally Open:1 -> Brake Selector2/Switch1:1
LINE Brake Selector2/Switch1:1 -> Brake Selector2/Out:1
LINE Brake Selector2:1 -> Goto5:1
LINE Brake Selector3/From1:1 -> Brake Selector3/Switch1:2
LINE Brake Selector3/Normally Close:1 -> Brake Selector3/Switch1:3
LINE Brake Selector3/Normally Open:1 -> Brake Selector3/Switch1:1
LINE Brake Selector3/Switch1:1 -> Brake Selector3/Out:1
LINE Brake Selector3:1 -> Goto3:1
LINE Brake Selector:1 -> Product1:1
LINE Brake Selector:1 -> Product:2
LINE Brake Selector:1 -> Scope20:1
LINE Bus Selector1:1 -> Product2:1
LINE Bus Selector1:1 -> Scope4:1
LINE Bus Selector1:2 -> Product2:2
LINE Bus Selector1:2 -> Scope6:1
LINE CCW Direction:1 -> Manual Switch:2
LINE CW Direction:1 -> Manual Switch:1
LINE Constant1:1 -> Brake Selector1:1
LINE Constant2:1 -> Manual Switch1:2
LINE Constant3:1 -> Brake Selector2:1
LINE Constant4:1 -> Brake Selector3:1
LINE Constant:1 -> Brake Selector:1
LINE Current Measurement1:1 -> Scope7:1
LINE Current Measurement2:1 -> Product3:1
LINE Current Measurement2:1 -> Product5:2
LINE Current Measurement2:1 -> Scope8:1
LINE Current Measurement2:rconn -> DC Machine1:lconn
LINE Current Measurement3:1 -> Scope22:1
LINE Current Measurement4:1 -> Scope23:1
LINE Current Measurement5:1 -> Scope24:1
LINE Current Measurement:1 -> Product4:1
LINE Current Measurement:1 -> Scope12:1
LINE Current Measurement:lconn -> Series RLC Branch1:rconn
LINE Current Measurement:lconn -> Series RLC Branch3:lconn
LINE DC Machine1:1 -> Bus Selector1:1
LINE DC Voltage Source1:lconn -> Current Measurement4:lconn
LINE DC Voltage Source:lconn -> DC Machine1:rconn
LINE DC Voltage Source:rconn -> DC Machine1:lconn
LINE Diode1:1 -> Scope2:1
LINE Diode1:rconn -> Q1:lconn
LINE Diode6:1 -> Scope25:1
LINE Diode6:rconn -> Current Measurement3:lconn
LINE Diode7:rconn -> AC Voltage Source3:lconn
LINE First-Order Filter:1 -> Display3:1
LINE First-Order Filter:1 -> Scope16:1
LINE From1:1 -> Q3:1
LINE From2:1 -> Q4:1
LINE From3:1 -> Manual Variant Sink:1
LINE From4:1 -> Gate Signals:1
LINE From5:1 -> Gate Signals:2
LINE From6:1 -> Gate Signals:3
LINE From7:1 -> Gate Signals:4
LINE From8:1 -> DC Machine1:1
LINE From:1 -> Q1:1
LINE Manual Switch1:1 -> PWM Generator:1
LINE Manual Switch2:1 -> Goto:1
LINE Manual Switch:1 -> Brake Selector2:2
LINE Manual Switch:1 -> NOT:1
LINE Manual Switch:1 -> Product:1
LINE Manual Variant Sink:1 -> Mosfet5:1
LINE Manual Variant Sink:2 -> Q2:1
LINE Mean1:1 -> Display1:1
LINE Mean1:1 -> Scope13:1
LINE Mean2:1 -> Display2:1
LINE Mean2:1 -> Scope15:1
LINE Mean3:1 -> Display4:1
LINE Mean3:1 -> Scope21:1
LINE Mean:1 -> Display:1
LINE Mosfet5:1 -> Scope18:1
LINE Mosfet5:lconn -> Series RLC Branch2:rconn
LINE NOT:1 -> Brake Selector1:2
LINE NOT:1 -> Product1:2
LINE PWM Generator1:1 -> Manual Switch2:2
LINE PWM Generator:1 -> Brake Selector:2
LINE Product1:1 -> Goto2:1
LINE Product2:1 -> Mean:1
LINE Product2:1 -> Scope10:1
LINE Product3:1 -> Mean1:1
LINE Product3:1 -> Scope11:1
LINE Product4:1 -> Mean2:1
LINE Product4:1 -> Scope14:1
LINE Product5:1 -> Mean3:1
LINE Product5:1 -> Scope9:1
LINE Product:1 -> Goto1:1
LINE Q1:1 -> Scope:1
LINE Q1:rconn -> Q2:lconn
LINE Q2:1 -> Scope3:1
LINE Q4:1 -> Scope5:1
LINE Q4:lconn -> Q3:rconn
LINE Ramp1:1 -> Saturation1:1
LINE Ramp2:1 -> Saturation2:1
LINE Ramp:1 -> Saturation:1
LINE Saturation1:1 -> Manual Switch1:1
LINE Saturation2:1 -> PWM Generator1:1
LINE Saturation:1 -> Brake Selector3:2
LINE Series RLC Branch3:rconn -> Current Measurement5:lconn
LINE Step:1 -> Manual Switch2:1
LINE Voltage Measurement1:1 -> First-Order Filter:1
LINE Voltage Measurement1:1 -> Product3:2
LINE Voltage Measurement1:1 -> Scope17:1
LINE Voltage Measurement2:1 -> Product4:2
LINE Voltage Measurement2:1 -> Scope1:1
LINE Voltage Measurement:1 -> Product5:1
LINE Voltage Measurement:1 -> Scope19:1
